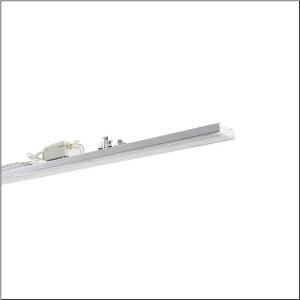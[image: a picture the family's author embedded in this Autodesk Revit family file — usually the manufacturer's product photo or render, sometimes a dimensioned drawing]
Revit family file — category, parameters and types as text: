
# Revit family: licross_11_recessed_ho_51te12dn4exm3c
name_source: partatom
category: Lighting Fixtures
units: mm (PartAtom-declared; Revit-internal decimal feet)

## family parameters
Cut with Voids When Loaded = No
Host = Face
Light Source = No
Part Type = Normal
Room Calculation Point = No
Round Connector Dimension = Use Diameter
Shared = No

## types (1)
- --- (1 x LED, 1000 lm, 7.2 W, 4000K)
    Apparent Load = 7 VA
    CIE Flux Codes = 66 91 98 100 100
    Color Rendering = 80
    Color Temperature = 4000K
    Default Elevation = 1800 mm
    Description = Licross 11 Recessed HO, luminaire insert, of sheet steel, galvanised, coil coated, white, length: 1.500mm, width: 66mm, height: 67mm, LED rated luminous flux: 14.030lm, light colour: 840, SDCM (Standard Deviation of Colour Matching)MacAdam ≤ 2 SDCM (initial), control gear: DALI 2 (for two DALI lines), with plug, 6-pole, with phase selection, for trunking rail, 14-core, mains connection: 220..240V, AC, 50/60Hz, rated input power: 81W, for trunking rail, 14-core, internal wiring halogen-free, for emergency light function, converter,control gear: single battery element, battery: LiFePO4, 9Ah, primary optical cover: cover, of PMMA, light emission: direct distribution, primary light characteristic: symmetric, protection rating (complete): IP54, insulation class (complete): insulation class I (protective earthing), certification: CE, UKCA, protection symbol: D if used in an environment with non-conductive dust loads with corresponding accessories, impact resistance: IK06, permissible ambient temperature for indoor applications: +5..+30°C, standard: EN 60598-2-22, LABS conformity tested according to VDMA 24364:2018-05, reducing of maximum allowable ambient temperature of 5°C with ceiling mounting, corresponds to IFS (International Featured Standards) requirements for safety and quality in the food industry, The light source and the operating device comply with the requirements of the Ecodesign Regulation (EU) 2019/2020 and are replaceable in accordance with this regulation, packaging unit: 1 piece
    Height = 58 mm
    Lamp = 1 x LED
    Lamp Light Flux = 1000 lm
    Lamp Power = 7.2 W
    Lamp count = 1
    Length = 1500 mm
    Luminous efficacy = 139 lm/W
    Manufacturer = Siteco
    ModVariant = No
    Model = 51TE12DN4EXM3C
    Mounting Place = Ceiling
    Mounting Type = Pendant
    Number of Poles = 1
    OnlyDefault = Yes
    Power Factor = 1
    Product Name = Licross 11 Recessed HO
    Product group = luminaire insert | ceiling pendant
    ProductGroupID = 901
    Protection Class = Protection class I
    Protection Degree = IP 54
    RLX_Detail_Level = 1
    RLX_Emergency_Light_Flux = 0 lm
    RLX_Emergency_Type = 0
    RLX_Emergency_Type_DB = No
    RlxData = <blob elided: 25265 chars, md5=b97111bc>
    Socket = socket
    Standby Power = 0 W
    System Light Flux = 1000 lm
    System Power = 7 W
    Type Comments = : emergency light operation: 3 h
    Type Image = l_1296930.jpg
    URL = http://relux.com
    VarID = @adj_095395
    Voltage = 0 V
    Weight = 0.00 kg
    Width = 66 mm

## geometry (parser evidence)
native form markers: Blend x4, Sweep x9
no freeform markers — native parametric forms only
